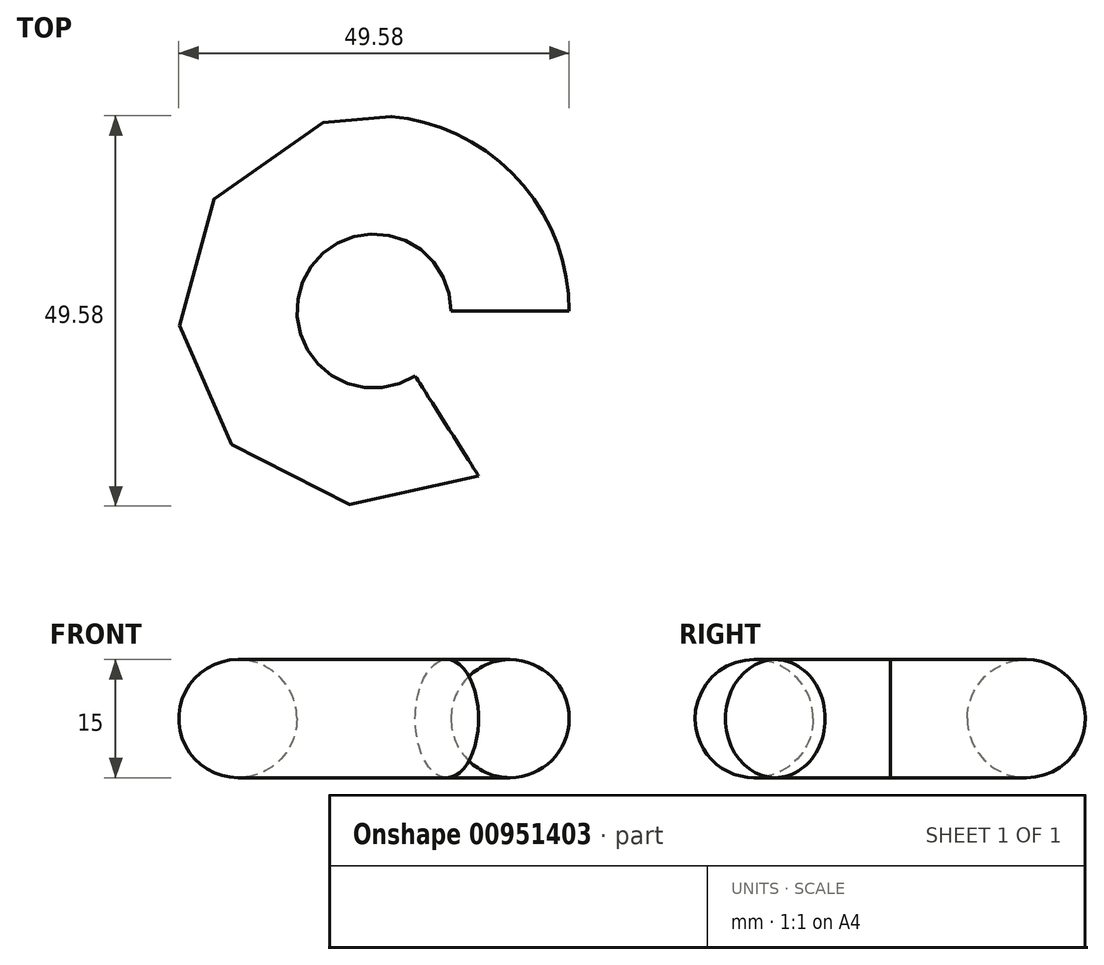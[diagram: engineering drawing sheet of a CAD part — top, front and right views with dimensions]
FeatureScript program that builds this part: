
annotation { "Feature Type Name" : "Feature", "Feature Type Description" : "" }
export const myFeature = defineFeature(function(context is Context, id is Id, definition is map)
    precondition{}
    {
        {
            var Q0;
            Q0=qCreatedBy(makeId("Top.planeOp"),FACE);
            var sketch = newSketch(context, id + "F0", { "sketchPlane" : qUnion([Q0])});
            skArc(sketch, "E0", {"start": v(25, 0) * mm, "mid": v(-21.9, 12.05) * mm, "end": v(13.4, -21.11) * mm});
            skSolve(sketch);
        }
        {
            var Q0;
            Q0=sQuery(id+"F0.wireOp",VERTEX,"E0.start");
            var Q1;
            Q1=sQuery(id+"F0.wireOp",EDGE,"E0");
            cPlane(context, id + "F1", {"entities" : qUnion([Q0, Q1]), "cplaneType" : CPlaneType.CURVE_POINT, "offset" : 25 * mm, "width" : 150 * mm, "height" : 150 * mm});
        }
        {
            var Q0;
            Q0=qCreatedBy(id+"F1.planeOp",FACE);
            var sketch = newSketch(context, id + "F2", { "sketchPlane" : qUnion([Q0])});
            skCircle(sketch, "E1", {"center": v(-17.3, 0) * mm, "radius": 7.5 * mm});
            skSolve(sketch);
        }
        {
            var Q0;
            Q0=makeQuery(id+"F2.imprint","IMPRINT",FACE,{"disambiguationData":[TD([[makeQuery(id+"F2.imprint","IMPRINT",EDGE,{"derivedFrom":sQuery(id+"F2.wireOp",EDGE,"E1")}),1.0]])]});
            var Q1;
            Q1 = qConstructionFilter(qBodyType(qCreatedBy(id + "F0" ,EDGE), BodyType.WIRE), ConstructionObject.NO);
            sweep(context, id + "F3", {"profiles" : qUnion([Q0]), "path" : qUnion([Q1])});
        }
    });
